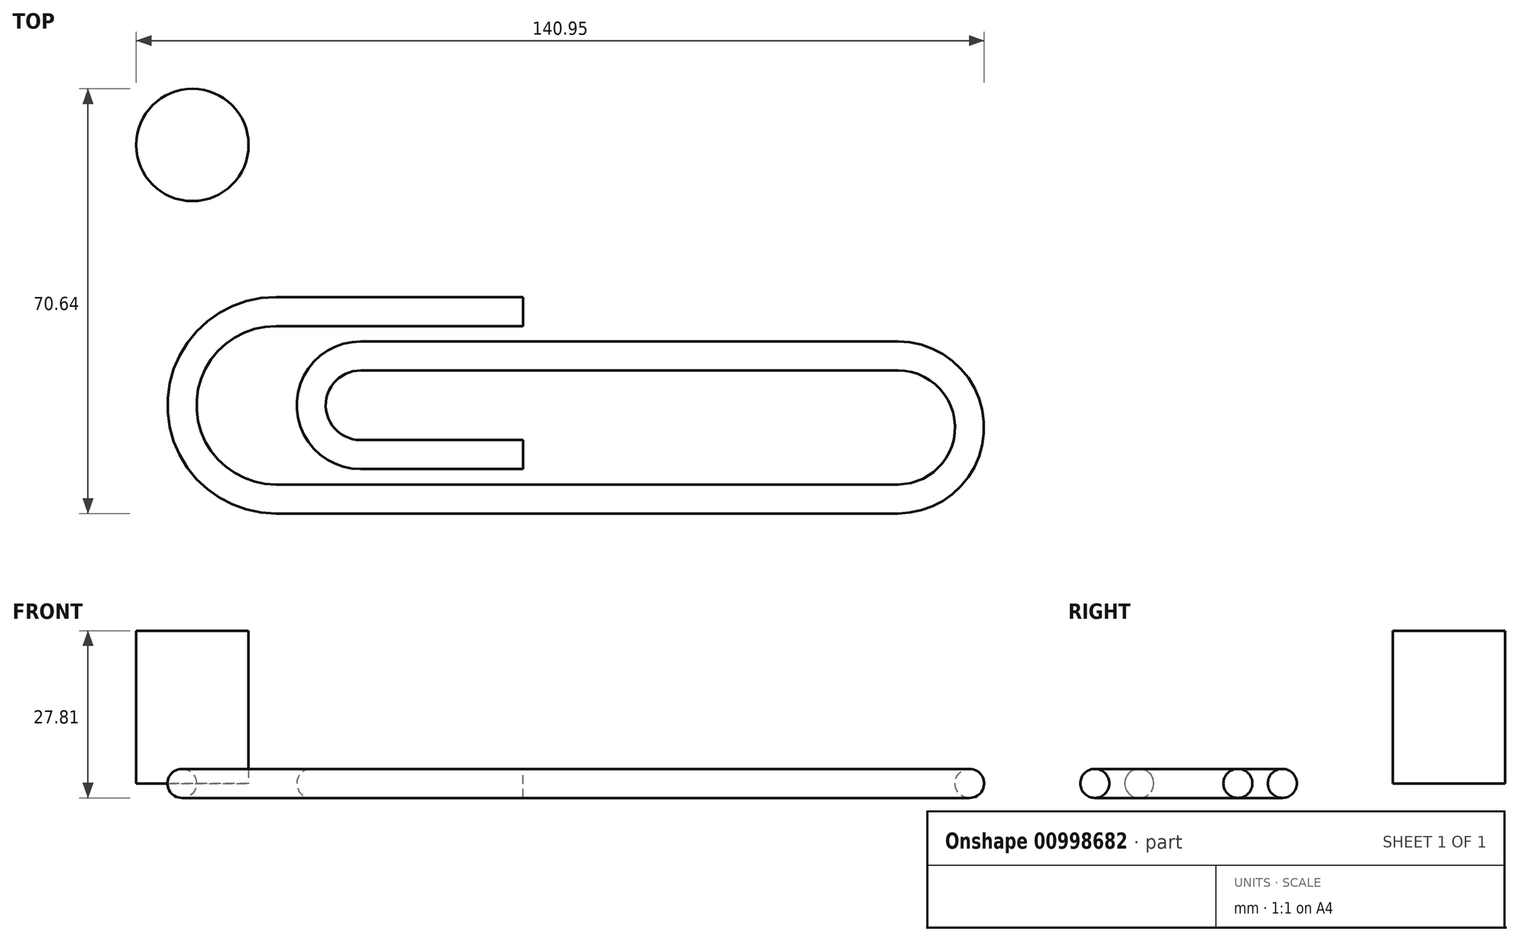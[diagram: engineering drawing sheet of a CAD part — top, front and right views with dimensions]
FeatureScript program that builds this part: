
annotation { "Feature Type Name" : "Feature", "Feature Type Description" : "" }
export const myFeature = defineFeature(function(context is Context, id is Id, definition is map)
    precondition{}
    {
        {
            var Q0;
            Q0=qCreatedBy(makeId("Top.planeOp"),FACE);
            var sketch = newSketch(context, id + "F0", { "sketchPlane" : qUnion([Q0])});
            skLineSegment(sketch, "E0", {"start": v(0, 19.86) * mm, "end": v(-41.1, 19.86) * mm});
            skArc(sketch, "E1", {"start": v(-41.1, 19.86) * mm, "mid": v(-56.69, 4.27) * mm, "end": v(-41.1, -11.31) * mm});
            skLineSegment(sketch, "E2", {"start": v(-41.1, -11.31) * mm, "end": v(62.35, -11.31) * mm});
            skArc(sketch, "E3", {"start": v(62.35, -11.31) * mm, "mid": v(74.24, 0.58) * mm, "end": v(62.35, 12.47) * mm});
            skLineSegment(sketch, "E4", {"start": v(62.35, 12.47) * mm, "end": v(-27, 12.47) * mm});
            skArc(sketch, "E5", {"start": v(-27, 12.47) * mm, "mid": v(-35.2, 4.27) * mm, "end": v(-27, -3.93) * mm});
            skLineSegment(sketch, "E6", {"start": v(-27, -3.93) * mm, "end": v(0, -3.93) * mm});
            skSolve(sketch);
        }
        {
            var Q0;
            Q0=qCreatedBy(makeId("Right.planeOp"),FACE);
            var sketch = newSketch(context, id + "F1", { "sketchPlane" : qUnion([Q0])});
            skCircle(sketch, "E7", {"center": v(19.86, 0) * mm, "radius": 2.41 * mm});
            skSolve(sketch);
        }
        {
            var Q0;
            Q0=makeQuery(id+"F1.imprint","IMPRINT",FACE,{"disambiguationData":[TD([[makeQuery(id+"F1.imprint","IMPRINT",EDGE,{"derivedFrom":sQuery(id+"F1.wireOp",EDGE,"E7")}),1.0]])]});
            var Q1;
            Q1=sQuery(id+"F0.wireOp",EDGE,"E0");
            var Q2;
            Q2=sQuery(id+"F0.wireOp",EDGE,"E1");
            var Q3;
            Q3=sQuery(id+"F0.wireOp",EDGE,"E2");
            var Q4;
            Q4=sQuery(id+"F0.wireOp",EDGE,"E3");
            var Q5;
            Q5=sQuery(id+"F0.wireOp",EDGE,"E4");
            var Q6;
            Q6=sQuery(id+"F0.wireOp",EDGE,"E5");
            var Q7;
            Q7=sQuery(id+"F0.wireOp",EDGE,"E6");
            sweep(context, id + "F2", {"profiles" : qUnion([Q0]), "path" : qUnion([Q1, Q2, Q3, Q4, Q5, Q6, Q7])});
        }
        {
            var Q0;
            Q0=qCreatedBy(makeId("Top.planeOp"),FACE);
            var sketch = newSketch(context, id + "F3", { "sketchPlane" : qUnion([Q0])});
            skCircle(sketch, "E8", {"center": v(-54.96, 47.57) * mm, "radius": 9.34 * mm});
            skSolve(sketch);
        }
        {
            var Q0;
            Q0=makeQuery(id+"F3.imprint","IMPRINT",FACE,{"disambiguationData":[TD([[makeQuery(id+"F3.imprint","IMPRINT",EDGE,{"derivedFrom":sQuery(id+"F3.wireOp",EDGE,"E8")}),1.0]])]});
            extrude(context, id + "F4", {"entities" : qUnion([Q0]), "operationType" : NewBodyOperationType.ADD, "depth" : 25.4 * mm, "offsetDistance" : 25.4 * mm});
        }
    });
